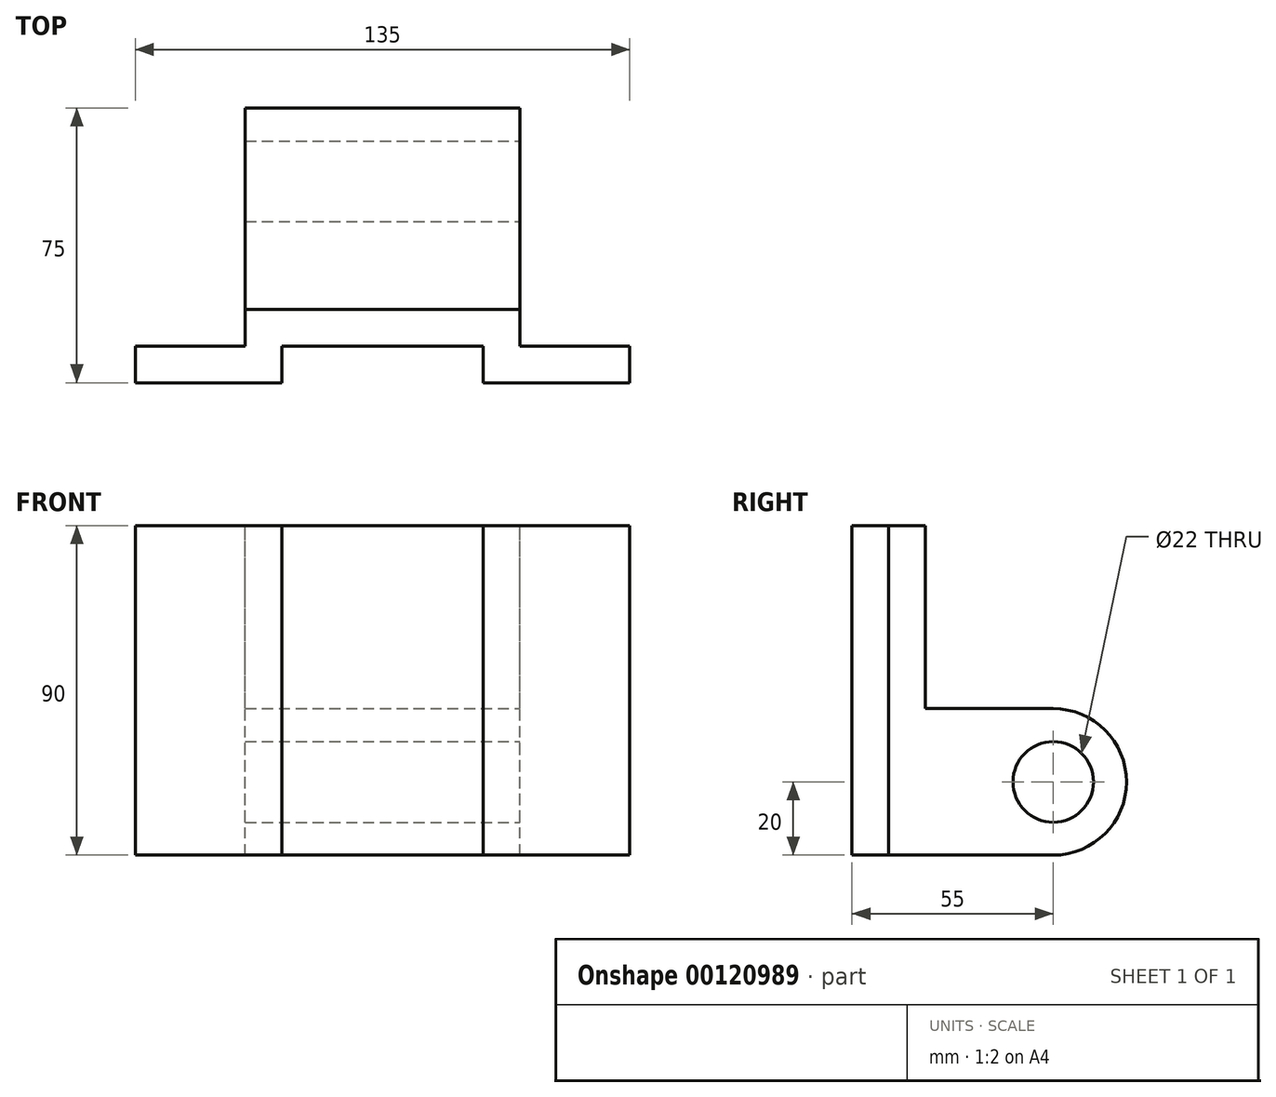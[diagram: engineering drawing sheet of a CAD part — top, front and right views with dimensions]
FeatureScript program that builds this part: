
annotation { "Feature Type Name" : "Feature", "Feature Type Description" : "" }
export const myFeature = defineFeature(function(context is Context, id is Id, definition is map)
    precondition{}
    {
        {
            var Q0;
            Q0=qCreatedBy(makeId("Top.planeOp"),FACE);
            var sketch = newSketch(context, id + "F0", { "sketchPlane" : qUnion([Q0])});
            skLineSegment(sketch, "E0.bottom", {"start": v(0, 0) * mm, "end": v(135, 0) * mm});
            skLineSegment(sketch, "E0.top", {"start": v(0, -10) * mm, "end": v(135, -10) * mm});
            skLineSegment(sketch, "E0.left", {"start": v(0, 0) * mm, "end": v(0, -10) * mm});
            skLineSegment(sketch, "E0.right", {"start": v(135, 0) * mm, "end": v(135, -10) * mm});
            skSolve(sketch);
        }
        {
            var Q0;
            Q0=makeQuery(id+"F0.imprint","IMPRINT",FACE,{"disambiguationData":[TD([[makeQuery(id+"F0.imprint","IMPRINT",EDGE,{"derivedFrom":sQuery(id+"F0.wireOp",EDGE,"E0.bottom")}),-1.0]])]});
            extrude(context, id + "F1", {"entities" : qUnion([Q0]), "depth" : 90 * mm});
        }
        {
            var Q0;
            Q0=qCreatedBy(makeId("Front.planeOp"),FACE);
            var sketch = newSketch(context, id + "F2", { "sketchPlane" : qUnion([Q0])});
            skLineSegment(sketch, "E1.bottom", {"start": v(105, 0) * mm, "end": v(30, 0) * mm});
            skLineSegment(sketch, "E1.top", {"start": v(105, 90) * mm, "end": v(30, 90) * mm});
            skLineSegment(sketch, "E1.left", {"start": v(105, 0) * mm, "end": v(105, 90) * mm});
            skLineSegment(sketch, "E1.right", {"start": v(30, 0) * mm, "end": v(30, 90) * mm});
            skSolve(sketch);
        }
        {
            var Q0;
            Q0=makeQuery(id+"F2.imprint","IMPRINT",FACE,{"disambiguationData":[TD([[makeQuery(id+"F2.imprint","IMPRINT",EDGE,{"derivedFrom":sQuery(id+"F2.wireOp",EDGE,"E1.bottom")}),-1.0]])]});
            extrude(context, id + "F3", {"entities" : qUnion([Q0]), "operationType" : NewBodyOperationType.ADD, "oppositeDirection" : true, "depth" : 10 * mm});
        }
        {
            var Q0;
            Q0=makeQuery(id+"F3.boolean.opBoolean","MERGE",FACE,{"derivedFrom":[makeQuery(id+"F1.opExtrude","CAP_FACE",FACE,{"disambiguationData":[OSD([sQuery(id+"F0.wireOp",EDGE,"E0.bottom"),sQuery(id+"F0.wireOp",EDGE,"E0.top"),sQuery(id+"F0.wireOp",EDGE,"E0.left"),sQuery(id+"F0.wireOp",EDGE,"E0.right")])],"isStart":false}),makeQuery(id+"F3.opExtrude","SWEPT_FACE",FACE,{"disambiguationData":[OSD([sQuery(id+"F2.wireOp",EDGE,"E1.top")])]})]});
            var sketch = newSketch(context, id + "F4", { "sketchPlane" : qUnion([Q0])});
            skLineSegment(sketch, "E2.bottom", {"start": v(40, -10) * mm, "end": v(95, -10) * mm});
            skLineSegment(sketch, "E2.left", {"start": v(40, -10) * mm, "end": v(40, 0) * mm});
            skLineSegment(sketch, "E2.right", {"start": v(95, -10) * mm, "end": v(95, 0) * mm});
            skLineSegment(sketch, "E3", {"start": v(40, 0) * mm, "end": v(95, 0) * mm});
            skSolve(sketch);
        }
        {
            var Q0;
            Q0=makeQuery(id+"F4.imprint","IMPRINT",FACE,{"disambiguationData":[TD([[makeQuery(id+"F4.imprint","IMPRINT",EDGE,{"derivedFrom":sQuery(id+"F4.wireOp",EDGE,"E2.bottom")}),1.0]])]});
            extrude(context, id + "F5", {"entities" : qUnion([Q0]), "operationType" : NewBodyOperationType.REMOVE, "endBound" : BoundingType.THROUGH_ALL, "oppositeDirection" : true, "depth" : 25 * mm});
        }
        {
            var Q0;
            Q0=makeQuery(id+"F3.opExtrude","SWEPT_FACE",FACE,{"disambiguationData":[OSD([sQuery(id+"F2.wireOp",EDGE,"E1.left")])]});
            var sketch = newSketch(context, id + "F6", { "sketchPlane" : qUnion([Q0])});
            skLineSegment(sketch, "E4.bottom", {"start": v(10, 0) * mm, "end": v(45, 0) * mm});
            skLineSegment(sketch, "E4.top", {"start": v(10, 40) * mm, "end": v(45, 40) * mm});
            skLineSegment(sketch, "E4.left", {"start": v(10, 0) * mm, "end": v(10, 40) * mm});
            skArc(sketch, "E5", {"start": v(45, 0) * mm, "mid": v(65, 20) * mm, "end": v(45, 40) * mm});
            skSolve(sketch);
        }
        {
            var Q0;
            Q0=makeQuery(id+"F6.imprint","IMPRINT",FACE,{"disambiguationData":[TD([[makeQuery(id+"F6.imprint","IMPRINT",EDGE,{"derivedFrom":sQuery(id+"F6.wireOp",EDGE,"E4.bottom")}),1.0]])]});
            extrude(context, id + "F7", {"entities" : qUnion([Q0]), "operationType" : NewBodyOperationType.ADD, "oppositeDirection" : true, "depth" : 75 * mm});
        }
        {
            var Q0;
            Q0=makeQuery(id+"F7.boolean.opBoolean","MERGE",FACE,{"derivedFrom":[makeQuery(id+"F3.opExtrude","SWEPT_FACE",FACE,{"disambiguationData":[OSD([sQuery(id+"F2.wireOp",EDGE,"E1.left")])]}),makeQuery(id+"F7.opExtrude","CAP_FACE",FACE,{"disambiguationData":[OSD([sQuery(id+"F6.wireOp",EDGE,"E4.bottom"),sQuery(id+"F6.wireOp",EDGE,"E4.top"),sQuery(id+"F6.wireOp",EDGE,"E4.left"),sQuery(id+"F6.wireOp",EDGE,"E5")])],"isStart":true})]});
            var sketch = newSketch(context, id + "F8", { "sketchPlane" : qUnion([Q0])});
            skSolve(sketch);
        }
        {
            var Q0;
            {var subQ0=sQuery(id+"F2.wireOp",EDGE,"E1.left");Q0=makeQuery(id+"F8.imprint","IMPRINT",FACE,{"disambiguationData":[TD([[makeQuery(id+"F8.imprint","IMPRINT",EDGE,{"derivedFrom":makeQuery(id+"F3.opExtrude","CAP_EDGE",EDGE,{"disambiguationData":[OSD([subQ0])],"isStart":true})}),-1.0]])]});}
            var sketch = newSketch(context, id + "F9", { "sketchPlane" : qUnion([Q0])});
            skPoint(sketch, "E6", {"position": v(45, 20) * mm});
            skSolve(sketch);
        }
        {
            var Q0;
            Q0=sQuery(id+"F9.wireOp",VERTEX,"E6");
            var Q1;
            Q1=makeQuery(id+"F1.opExtrude","SWEPT_BODY",BODY,{"disambiguationData":[OSD([sQuery(id+"F0.wireOp",EDGE,"E0.bottom"),sQuery(id+"F0.wireOp",EDGE,"E0.top"),sQuery(id+"F0.wireOp",EDGE,"E0.left"),sQuery(id+"F0.wireOp",EDGE,"E0.right")])]});
            hole(context, id + "F10", {"style" : HoleStyle.SIMPLE, "endStyle" : HoleEndStyle.THROUGH, "holeDiameter" : 22 * mm, "locations" : qUnion([Q0]), "scope" : qUnion([Q1]), "isTappedThrough" : true});
        }
    });
